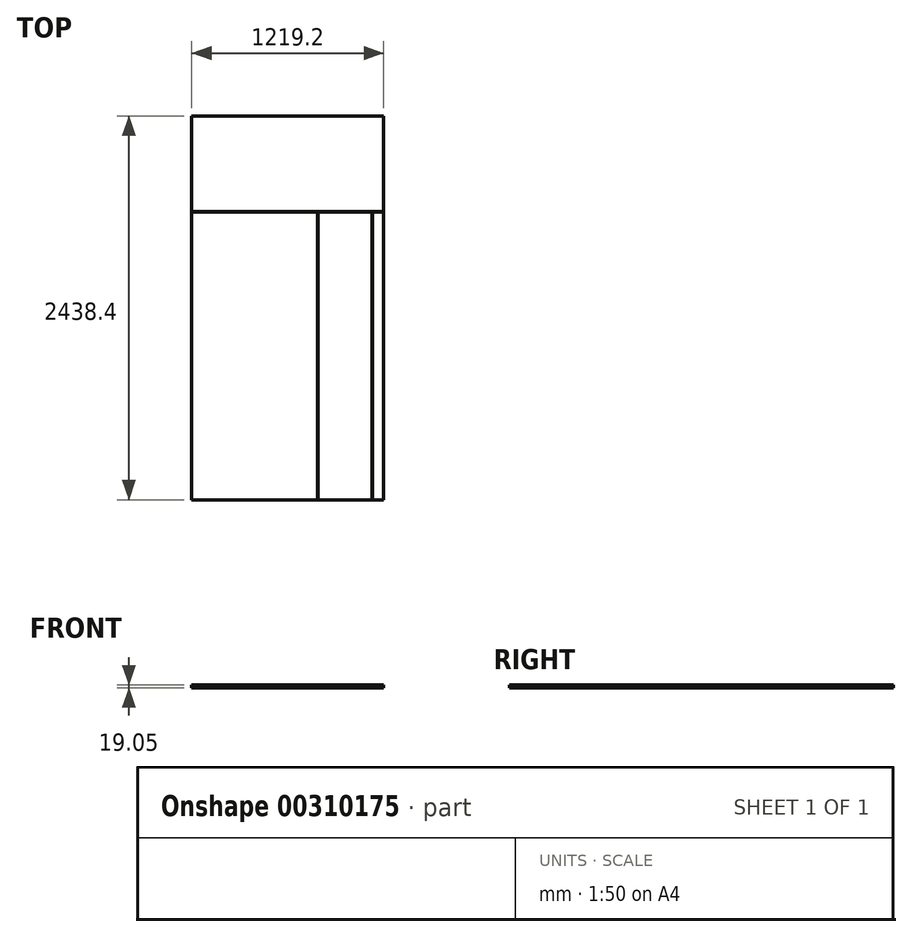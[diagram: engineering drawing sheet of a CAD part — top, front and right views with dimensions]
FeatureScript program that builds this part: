
annotation { "Feature Type Name" : "Feature", "Feature Type Description" : "" }
export const myFeature = defineFeature(function(context is Context, id is Id, definition is map)
    precondition{}
    {
        {
            var Q0;
            Q0=qCreatedBy(makeId("Top.planeOp"),FACE);
            var sketch = newSketch(context, id + "F0", { "sketchPlane" : qUnion([Q0])});
            skLineSegment(sketch, "E0.bottom", {"start": v(-609.6, 1219.2) * mm, "end": v(609.6, 1219.2) * mm});
            skLineSegment(sketch, "E0.top", {"start": v(-609.6, -1219.2) * mm, "end": v(609.6, -1219.2) * mm});
            skLineSegment(sketch, "E0.left", {"start": v(-609.6, 1219.2) * mm, "end": v(-609.6, -1219.2) * mm});
            skLineSegment(sketch, "E0.right", {"start": v(609.6, 1219.2) * mm, "end": v(609.6, -1219.2) * mm});
            skLineSegment(sketch, "E1", {"start": v(0, -1219.2) * mm, "end": v(0, 1219.2) * mm, "construction": true});
            skLineSegment(sketch, "E2", {"start": v(-609.6, 0) * mm, "end": v(609.6, 0) * mm, "construction": true});
            skSolve(sketch);
        }
        {
            var Q0;
            Q0 = qSketchRegion(id + "F0", true);
            extrude(context, id + "F1", {"entities" : qUnion([Q0]), "depth" : 19.05 * mm});
        }
        {
            var Q0;
            Q0=makeQuery(id+"F1.opExtrude","CAP_FACE",FACE,{"disambiguationData":[OSD([sQuery(id+"F0.wireOp",EDGE,"E0.bottom"),sQuery(id+"F0.wireOp",EDGE,"E0.top"),sQuery(id+"F0.wireOp",EDGE,"E0.left"),sQuery(id+"F0.wireOp",EDGE,"E0.right")])],"isStart":false});
            var sketch = newSketch(context, id + "F2", { "sketchPlane" : qUnion([Q0])});
            skLineSegment(sketch, "E3.bottom", {"start": v(-609.6, 609.6) * mm, "end": v(609.6, 609.6) * mm});
            skLineSegment(sketch, "E3.top", {"start": v(-609.6, 612.78) * mm, "end": v(609.6, 612.78) * mm});
            skLineSegment(sketch, "E3.left", {"start": v(-609.6, 609.6) * mm, "end": v(-609.6, 612.78) * mm});
            skLineSegment(sketch, "E3.right", {"start": v(609.6, 609.6) * mm, "end": v(609.6, 612.78) * mm});
            skLineSegment(sketch, "E4.bottom", {"start": v(190.5, -1219.2) * mm, "end": v(193.67, -1219.2) * mm});
            skLineSegment(sketch, "E4.top", {"start": v(190.5, 609.6) * mm, "end": v(193.67, 609.6) * mm});
            skLineSegment(sketch, "E4.left", {"start": v(190.5, -1219.2) * mm, "end": v(190.5, 609.6) * mm});
            skLineSegment(sketch, "E4.right", {"start": v(193.67, -1219.2) * mm, "end": v(193.67, 609.6) * mm});
            skLineSegment(sketch, "E5.bottom", {"start": v(536.57, 609.6) * mm, "end": v(539.75, 609.6) * mm});
            skLineSegment(sketch, "E5.top", {"start": v(536.58, -1219.2) * mm, "end": v(539.75, -1219.2) * mm});
            skLineSegment(sketch, "E5.left", {"start": v(536.57, 609.6) * mm, "end": v(536.58, -1219.2) * mm});
            skLineSegment(sketch, "E5.right", {"start": v(539.75, 609.6) * mm, "end": v(539.75, -1219.2) * mm});
            skSolve(sketch);
        }
        {
            var Q0;
            Q0 = qSketchRegion(id + "F2", true);
            extrude(context, id + "F3", {"entities" : qUnion([Q0]), "operationType" : NewBodyOperationType.REMOVE, "endBound" : BoundingType.UP_TO_NEXT, "oppositeDirection" : true, "depth" : 25.4 * mm});
        }
    });
